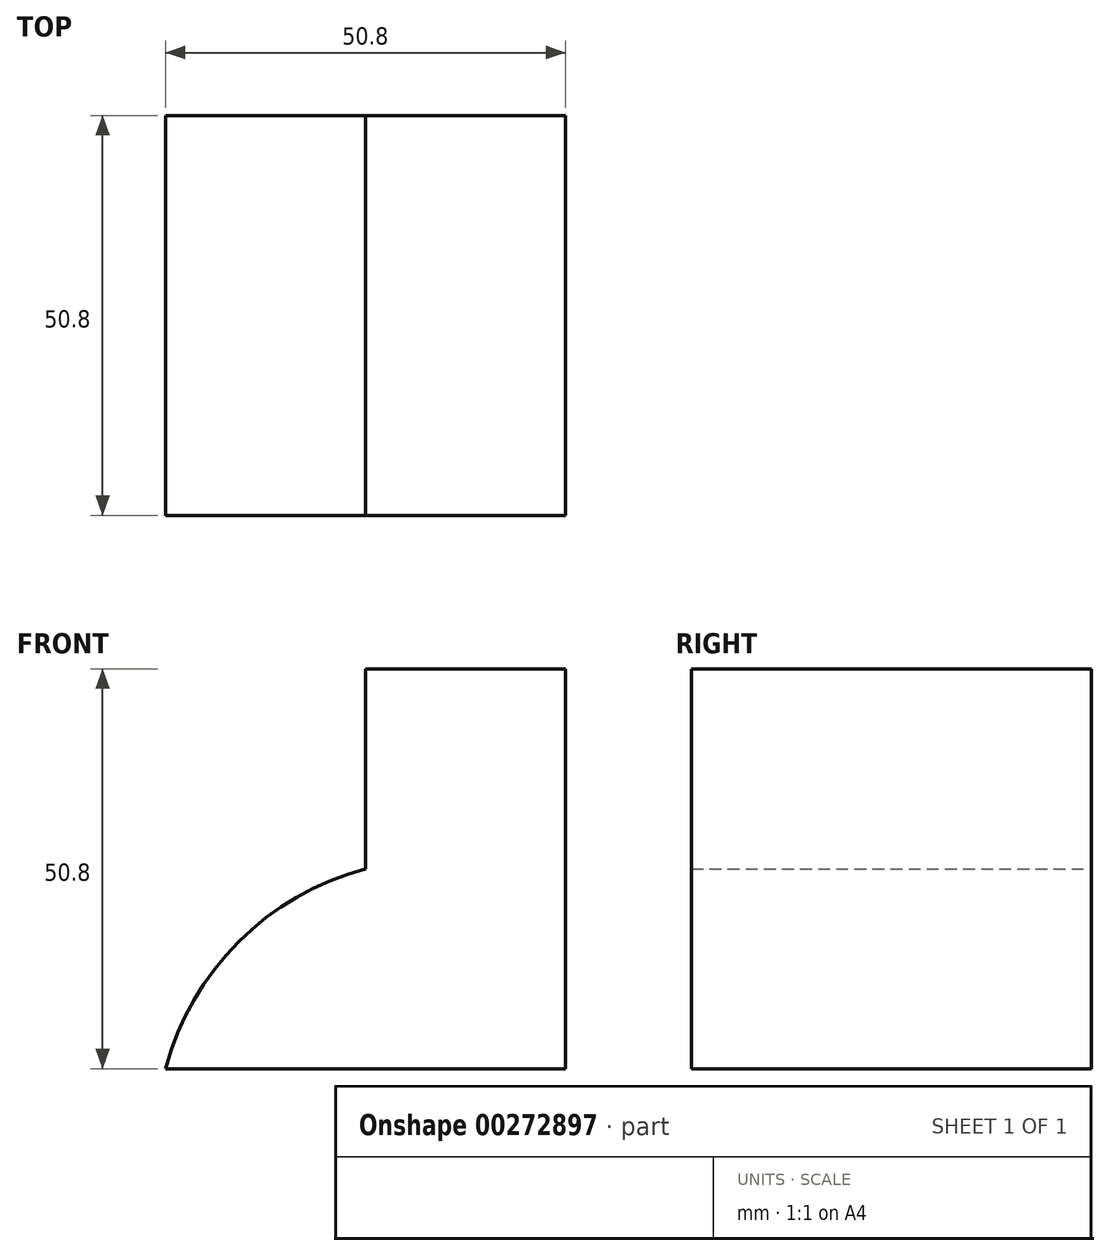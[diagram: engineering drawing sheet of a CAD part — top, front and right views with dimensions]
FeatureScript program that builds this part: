
annotation { "Feature Type Name" : "Feature", "Feature Type Description" : "" }
export const myFeature = defineFeature(function(context is Context, id is Id, definition is map)
    precondition{}
    {
        {
            var Q0;
            Q0=qCreatedBy(makeId("Front.planeOp"),FACE);
            var sketch = newSketch(context, id + "F0", { "sketchPlane" : qUnion([Q0])});
            skLineSegment(sketch, "E0", {"start": v(0, 0) * mm, "end": v(0, 50.8) * mm});
            skLineSegment(sketch, "E1", {"start": v(-25.4, 50.8) * mm, "end": v(0, 50.8) * mm});
            skLineSegment(sketch, "E2", {"start": v(-25.4, 50.8) * mm, "end": v(-25.4, 25.4) * mm});
            skLineSegment(sketch, "E3", {"start": v(0, 0) * mm, "end": v(-50.8, 0) * mm});
            skArc(sketch, "E4", {"start": v(-25.4, 25.4) * mm, "mid": v(-41.52, 16.12) * mm, "end": v(-50.8, 0) * mm});
            skSolve(sketch);
        }
        {
            var Q0;
            Q0 = qSketchRegion(id + "F0", true);
            extrude(context, id + "F1", {"entities" : qUnion([Q0]), "depth" : 50.8 * mm});
        }
    });
